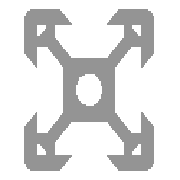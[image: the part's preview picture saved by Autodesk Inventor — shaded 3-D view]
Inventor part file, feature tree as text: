
AUTODESK INVENTOR PART (.ipt)
format: ipt  version: 2013 SP2 (Build 170200200, 200)  size: 171,520 bytes
history: native  units: mm
features: other x3, sketch x3, plane x1
ambient origin geometry x8: Origin, YZ Plane, XZ Plane, XY Plane, X Axis, Y Axis, Z Axis, Center Point
bodies: Solid1 (feature_tree), Body (feature_tree)
feature tree (7):
  other  "Driven Length"
  other  "Start Plane"
  other  "End Plane"
  sketch  "Sketch1"  dims[d2=4.2mm]
  sketch  "Sketch4"  dims[d3=1.5mm]
  plane  "Work Plane4"
  sketch  "Sketch5"  dims[d4=1.64mm d5=1.8mm d6=5.68mm d7=1.8mm d9=1.5mm d12=-0.0mm d13=20.0mm d14=0.13mm d15=0.0mm d18=90.0deg d17=20.0mm]
